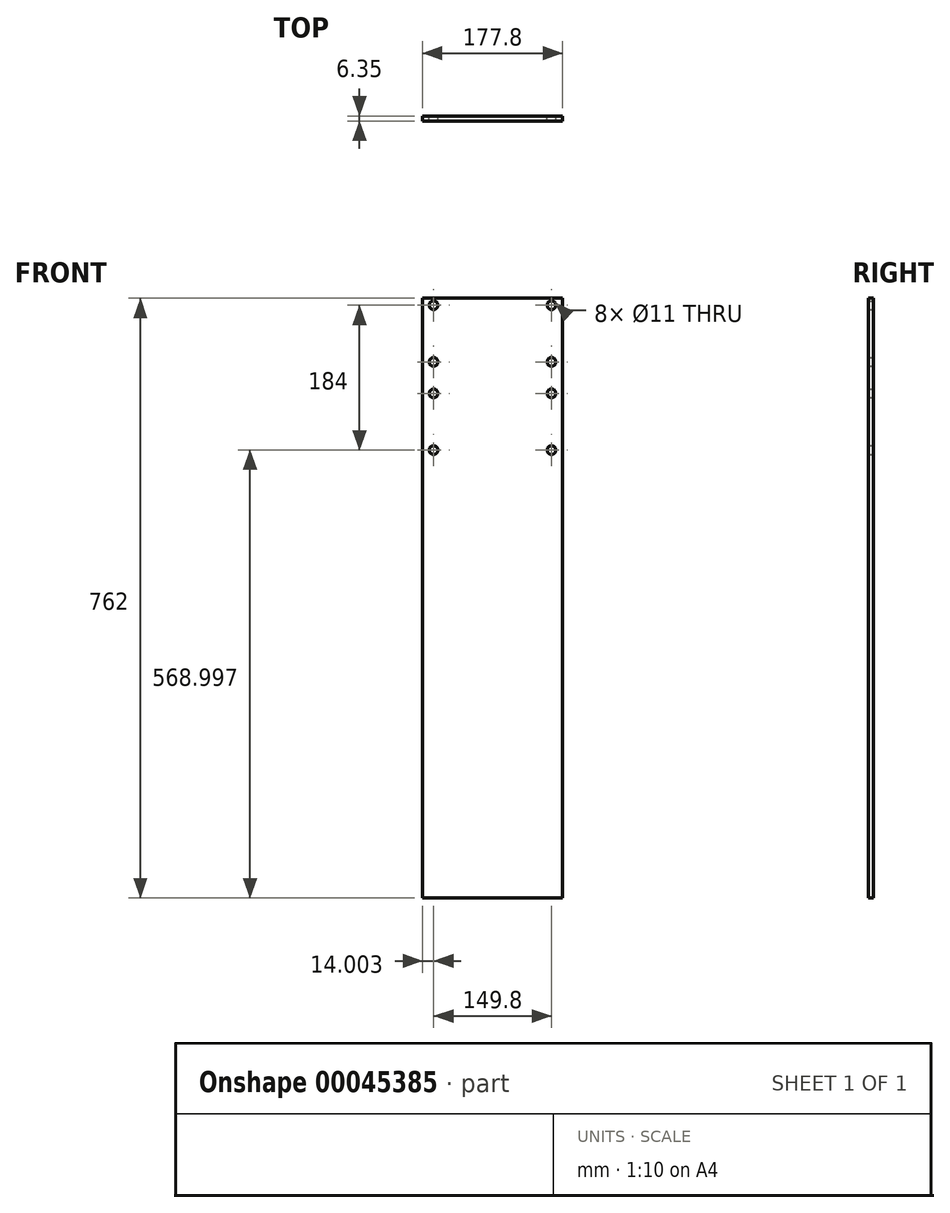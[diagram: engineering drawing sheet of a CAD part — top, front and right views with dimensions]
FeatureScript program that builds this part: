
annotation { "Feature Type Name" : "Feature", "Feature Type Description" : "" }
export const myFeature = defineFeature(function(context is Context, id is Id, definition is map)
    precondition{}
    {
        {
            var Q0;
            Q0=qCreatedBy(makeId("Front.planeOp"),FACE);
            var sketch = newSketch(context, id + "F0", { "sketchPlane" : qUnion([Q0])});
            skLineSegment(sketch, "E0.bottom", {"start": v(-305.03, 117.56) * mm, "end": v(-127.23, 117.56) * mm});
            skLineSegment(sketch, "E0.top", {"start": v(-305.03, -644.44) * mm, "end": v(-127.23, -644.44) * mm});
            skLineSegment(sketch, "E0.left", {"start": v(-305.03, 117.56) * mm, "end": v(-305.03, -644.44) * mm});
            skLineSegment(sketch, "E0.right", {"start": v(-127.23, 117.56) * mm, "end": v(-127.23, -644.44) * mm});
            skCircle(sketch, "E1", {"center": v(-141.23, 108.56) * mm, "radius": 5.5 * mm});
            skCircle(sketch, "E2", {"center": v(-141.23, 36.56) * mm, "radius": 5.5 * mm});
            skCircle(sketch, "E3", {"center": v(-141.23, -3.44) * mm, "radius": 5.5 * mm});
            skCircle(sketch, "E4", {"center": v(-141.23, -75.44) * mm, "radius": 5.5 * mm});
            skCircle(sketch, "E5", {"center": v(-291.03, 108.56) * mm, "radius": 5.5 * mm});
            skCircle(sketch, "E6", {"center": v(-291.03, -3.44) * mm, "radius": 5.5 * mm});
            skCircle(sketch, "E7", {"center": v(-291.03, -75.44) * mm, "radius": 5.5 * mm});
            skCircle(sketch, "E8", {"center": v(-291.03, 36.56) * mm, "radius": 5.5 * mm});
            skSolve(sketch);
        }
        {
            var Q0;
            Q0=makeQuery(id+"F0.imprint","IMPRINT",FACE,{"disambiguationData":[TD([[makeQuery(id+"F0.imprint","IMPRINT",EDGE,{"derivedFrom":sQuery(id+"F0.wireOp",EDGE,"E0.top")}),1.0]])]});
            extrude(context, id + "F1", {"entities" : qUnion([Q0]), "depth" : 6.35 * mm});
        }
    });
